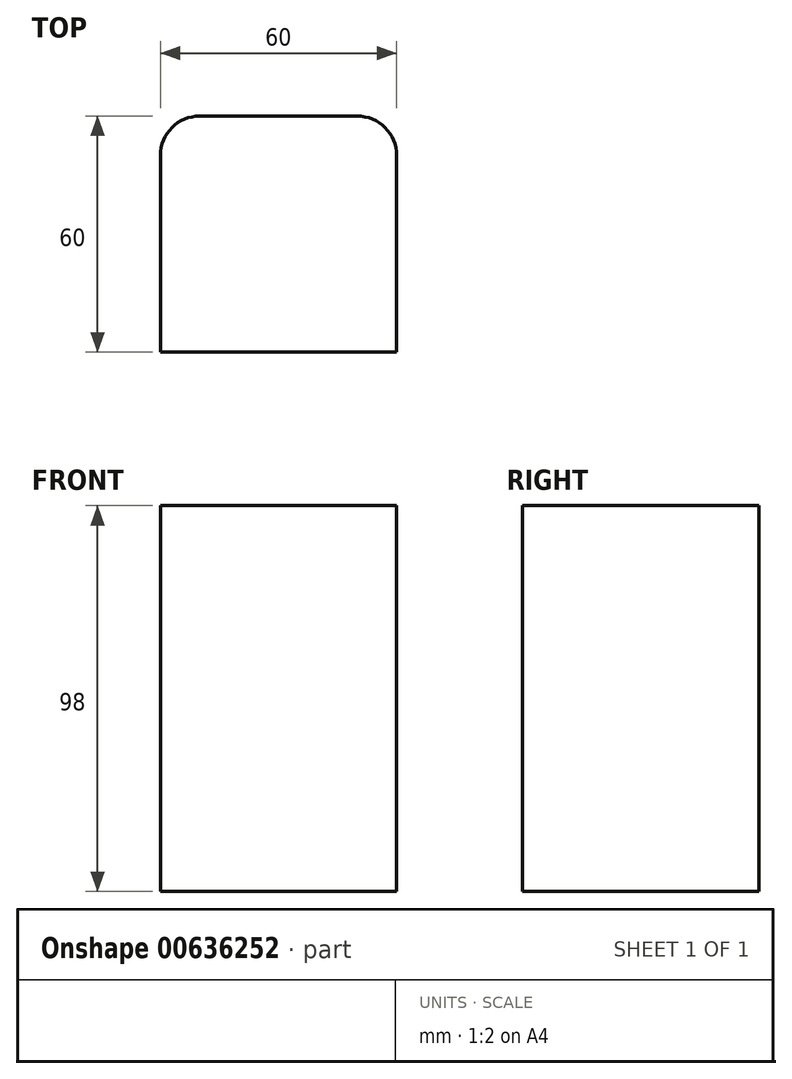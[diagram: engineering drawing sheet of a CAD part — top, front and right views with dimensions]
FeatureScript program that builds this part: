
annotation { "Feature Type Name" : "Feature", "Feature Type Description" : "" }
export const myFeature = defineFeature(function(context is Context, id is Id, definition is map)
    precondition{}
    {
        {
            var Q0;
            Q0=qCreatedBy(makeId("Front.planeOp"),FACE);
            var sketch = newSketch(context, id + "F0", { "sketchPlane" : qUnion([Q0])});
            skLineSegment(sketch, "E0.bottom", {"start": v(29.81, -74.97) * mm, "end": v(-30.19, -74.97) * mm});
            skLineSegment(sketch, "E0.top", {"start": v(29.81, 23.03) * mm, "end": v(-30.19, 23.03) * mm});
            skLineSegment(sketch, "E0.left", {"start": v(29.81, -74.97) * mm, "end": v(29.81, 23.03) * mm});
            skLineSegment(sketch, "E0.right", {"start": v(-30.19, -74.97) * mm, "end": v(-30.19, 23.03) * mm});
            skPoint(sketch, "E1.0", {"position": v(0, 0) * mm});
            skSolve(sketch);
        }
        {
            var Q0;
            Q0 = qSketchRegion(id + "F0", true);
            extrude(context, id + "F1", {"entities" : qUnion([Q0]), "depth" : 60 * mm, "offsetDistance" : 25 * mm});
        }
        {
            var Q0;
            Q0=makeQuery(id+"F1.opExtrude","CAP_EDGE",EDGE,{"disambiguationData":[OSD([sQuery(id+"F0.wireOp",EDGE,"E0.left")])],"isStart":true});
            var Q1;
            Q1=makeQuery(id+"F1.opExtrude","CAP_EDGE",EDGE,{"disambiguationData":[OSD([sQuery(id+"F0.wireOp",EDGE,"E0.right")])],"isStart":true});
            fillet(context, id + "F2", {"entities" : qUnion([Q0, Q1]), "radius" : 10 * mm, "tangentPropagation" : true, "allowEdgeOverflow" : false});
        }
    });
